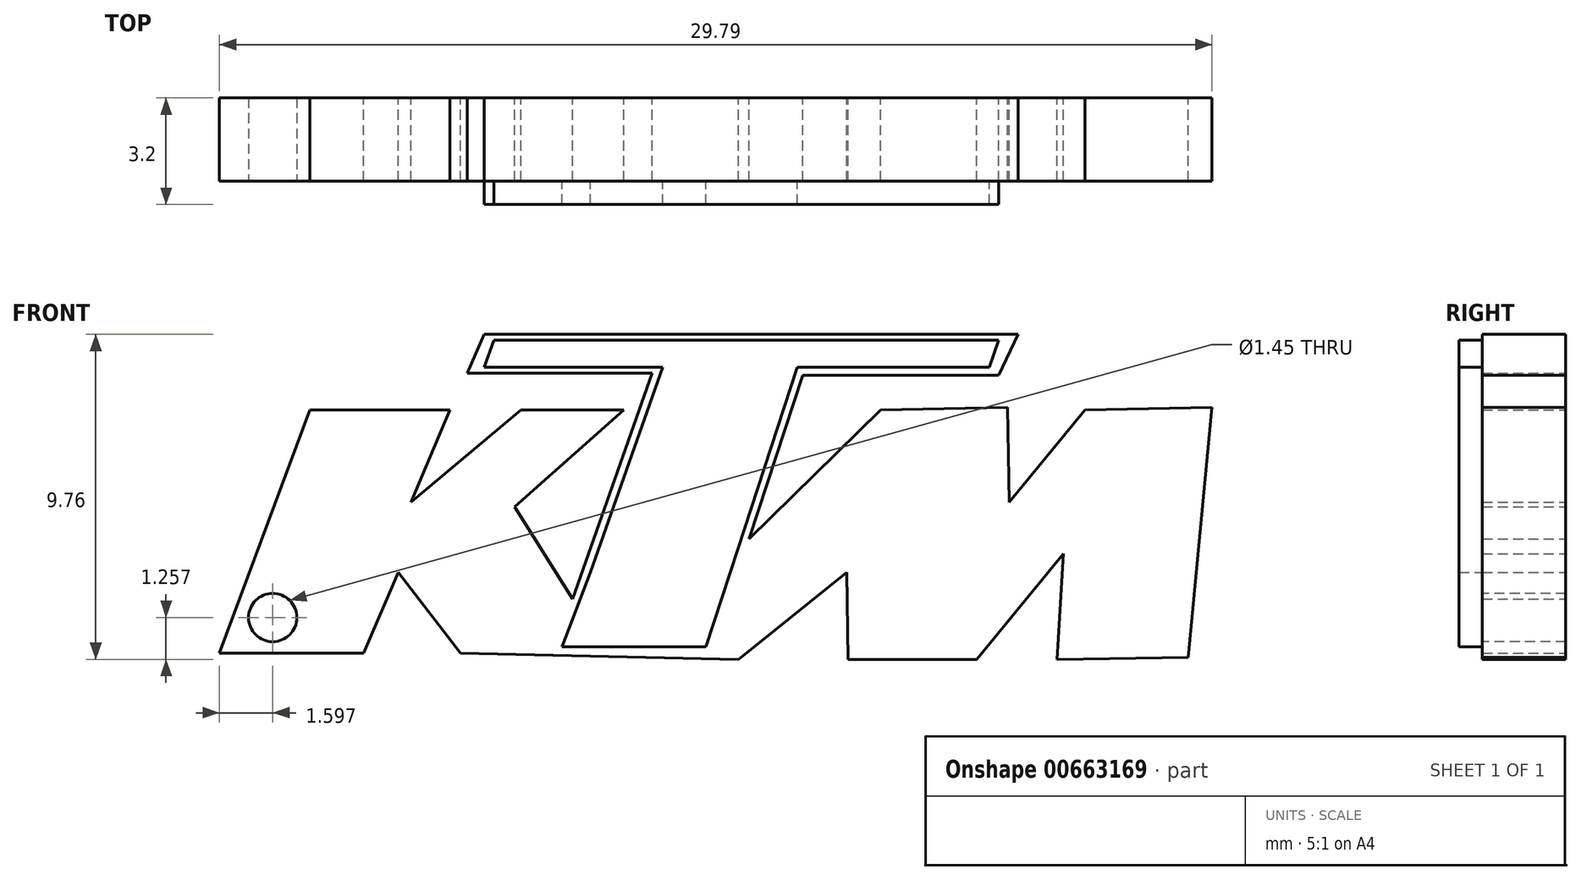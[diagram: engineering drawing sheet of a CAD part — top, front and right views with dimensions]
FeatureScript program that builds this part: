
annotation { "Feature Type Name" : "Feature", "Feature Type Description" : "" }
export const myFeature = defineFeature(function(context is Context, id is Id, definition is map)
    precondition{}
    {
        {
            var Q0;
            Q0=qCreatedBy(makeId("Front.planeOp"),FACE);
            var sketch = newSketch(context, id + "F0", { "sketchPlane" : qUnion([Q0])});
            skLineSegment(sketch, "E0", {"start": v(-12.13, -2.42) * mm, "end": v(-9.42, 4.88) * mm});
            skLineSegment(sketch, "E1", {"start": v(-9.42, 4.88) * mm, "end": v(-5.22, 4.88) * mm});
            skLineSegment(sketch, "E2", {"start": v(-5.22, 4.88) * mm, "end": v(-6.38, 2.1) * mm});
            skLineSegment(sketch, "E3", {"start": v(-6.38, 2.1) * mm, "end": v(-3.08, 4.88) * mm});
            skLineSegment(sketch, "E4", {"start": v(-3.08, 4.88) * mm, "end": v(0, 4.88) * mm});
            skLineSegment(sketch, "E5", {"start": v(0, 4.88) * mm, "end": v(-3.28, 1.98) * mm});
            skLineSegment(sketch, "E6", {"start": v(-3.28, 1.98) * mm, "end": v(-1.53, -0.8) * mm});
            skLineSegment(sketch, "E7", {"start": v(-1.53, -0.8) * mm, "end": v(0.86, 5.98) * mm});
            skLineSegment(sketch, "E8", {"start": v(0.86, 5.98) * mm, "end": v(-4.7, 5.98) * mm});
            skLineSegment(sketch, "E9", {"start": v(-4.7, 5.98) * mm, "end": v(-4.18, 7.15) * mm});
            skLineSegment(sketch, "E10", {"start": v(-4.18, 7.15) * mm, "end": v(11.84, 7.15) * mm});
            skLineSegment(sketch, "E11", {"start": v(11.84, 7.15) * mm, "end": v(11.26, 5.92) * mm});
            skLineSegment(sketch, "E12", {"start": v(11.26, 5.92) * mm, "end": v(5.38, 5.92) * mm});
            skLineSegment(sketch, "E13", {"start": v(5.38, 5.92) * mm, "end": v(3.77, 1) * mm});
            skLineSegment(sketch, "E14", {"start": v(3.77, 1) * mm, "end": v(7.7, 4.88) * mm});
            skLineSegment(sketch, "E15", {"start": v(11.52, 4.95) * mm, "end": v(7.7, 4.88) * mm});
            skLineSegment(sketch, "E16", {"start": v(11.52, 4.95) * mm, "end": v(11.57, 2.11) * mm});
            skLineSegment(sketch, "E17", {"start": v(11.57, 2.11) * mm, "end": v(13.85, 4.88) * mm});
            skLineSegment(sketch, "E18", {"start": v(13.85, 4.88) * mm, "end": v(17.66, 4.95) * mm});
            skLineSegment(sketch, "E19", {"start": v(17.66, 4.95) * mm, "end": v(16.95, -2.55) * mm});
            skLineSegment(sketch, "E20", {"start": v(16.95, -2.55) * mm, "end": v(13.01, -2.61) * mm});
            skLineSegment(sketch, "E21", {"start": v(13.2, 0.56) * mm, "end": v(13.01, -2.61) * mm});
            skLineSegment(sketch, "E22", {"start": v(13.2, 0.56) * mm, "end": v(10.6, -2.61) * mm});
            skLineSegment(sketch, "E23", {"start": v(6.74, -2.61) * mm, "end": v(10.6, -2.61) * mm});
            skLineSegment(sketch, "E24", {"start": v(6.74, -2.61) * mm, "end": v(6.7, 0) * mm});
            skLineSegment(sketch, "E25", {"start": v(6.7, 0) * mm, "end": v(3.44, -2.61) * mm});
            skLineSegment(sketch, "E26", {"start": v(-4.9, -2.42) * mm, "end": v(3.44, -2.61) * mm});
            skLineSegment(sketch, "E27", {"start": v(-6.77, 0) * mm, "end": v(-4.9, -2.42) * mm});
            skLineSegment(sketch, "E28", {"start": v(-7.8, -2.42) * mm, "end": v(-6.77, 0) * mm});
            skLineSegment(sketch, "E29", {"start": v(-12.13, -2.42) * mm, "end": v(-7.8, -2.42) * mm});
            skSolve(sketch);
        }
        {
            var Q0;
            Q0=makeQuery(id+"F0.imprint","IMPRINT",FACE,{"disambiguationData":[TD([[makeQuery(id+"F0.imprint","IMPRINT",EDGE,{"derivedFrom":sQuery(id+"F0.wireOp",EDGE,"E0")}),-1.0]])]});
            extrude(context, id + "F1", {"entities" : qUnion([Q0]), "depth" : 2.5 * mm, "offsetDistance" : 25 * mm});
        }
        {
            var Q0;
            Q0=makeQuery(id+"F1.opExtrude","CAP_FACE",FACE,{"disambiguationData":[OSD([sQuery(id+"F0.wireOp",EDGE,"E0"),sQuery(id+"F0.wireOp",EDGE,"E1"),sQuery(id+"F0.wireOp",EDGE,"E2"),sQuery(id+"F0.wireOp",EDGE,"E3"),sQuery(id+"F0.wireOp",EDGE,"E4"),sQuery(id+"F0.wireOp",EDGE,"E5"),sQuery(id+"F0.wireOp",EDGE,"E6"),sQuery(id+"F0.wireOp",EDGE,"E7"),sQuery(id+"F0.wireOp",EDGE,"E8"),sQuery(id+"F0.wireOp",EDGE,"E9"),sQuery(id+"F0.wireOp",EDGE,"E10"),sQuery(id+"F0.wireOp",EDGE,"E11"),sQuery(id+"F0.wireOp",EDGE,"E12"),sQuery(id+"F0.wireOp",EDGE,"E13"),sQuery(id+"F0.wireOp",EDGE,"E14"),sQuery(id+"F0.wireOp",EDGE,"E15"),sQuery(id+"F0.wireOp",EDGE,"E16"),sQuery(id+"F0.wireOp",EDGE,"E17"),sQuery(id+"F0.wireOp",EDGE,"E18"),sQuery(id+"F0.wireOp",EDGE,"E19"),sQuery(id+"F0.wireOp",EDGE,"E20"),sQuery(id+"F0.wireOp",EDGE,"E21"),sQuery(id+"F0.wireOp",EDGE,"E22"),sQuery(id+"F0.wireOp",EDGE,"E23"),sQuery(id+"F0.wireOp",EDGE,"E24"),sQuery(id+"F0.wireOp",EDGE,"E25"),sQuery(id+"F0.wireOp",EDGE,"E26"),sQuery(id+"F0.wireOp",EDGE,"E27"),sQuery(id+"F0.wireOp",EDGE,"E28"),sQuery(id+"F0.wireOp",EDGE,"E29")])],"isStart":false});
            var sketch = newSketch(context, id + "F2", { "sketchPlane" : qUnion([Q0])});
            skCircle(sketch, "E30", {"center": v(-10.53, -1.35) * mm, "radius": 0.72 * mm});
            skSolve(sketch);
        }
        {
            var Q0;
            Q0 = qSketchRegion(id + "F2", true);
            extrude(context, id + "F3", {"entities" : qUnion([Q0]), "operationType" : NewBodyOperationType.REMOVE, "endBound" : BoundingType.UP_TO_NEXT, "oppositeDirection" : true, "depth" : 25 * mm, "offsetDistance" : 25 * mm});
        }
        {
            var Q0;
            Q0=makeQuery(id+"F1.opExtrude","CAP_FACE",FACE,{"disambiguationData":[OSD([sQuery(id+"F0.wireOp",EDGE,"E0"),sQuery(id+"F0.wireOp",EDGE,"E1"),sQuery(id+"F0.wireOp",EDGE,"E2"),sQuery(id+"F0.wireOp",EDGE,"E3"),sQuery(id+"F0.wireOp",EDGE,"E4"),sQuery(id+"F0.wireOp",EDGE,"E5"),sQuery(id+"F0.wireOp",EDGE,"E6"),sQuery(id+"F0.wireOp",EDGE,"E7"),sQuery(id+"F0.wireOp",EDGE,"E8"),sQuery(id+"F0.wireOp",EDGE,"E9"),sQuery(id+"F0.wireOp",EDGE,"E10"),sQuery(id+"F0.wireOp",EDGE,"E11"),sQuery(id+"F0.wireOp",EDGE,"E12"),sQuery(id+"F0.wireOp",EDGE,"E13"),sQuery(id+"F0.wireOp",EDGE,"E14"),sQuery(id+"F0.wireOp",EDGE,"E15"),sQuery(id+"F0.wireOp",EDGE,"E16"),sQuery(id+"F0.wireOp",EDGE,"E17"),sQuery(id+"F0.wireOp",EDGE,"E18"),sQuery(id+"F0.wireOp",EDGE,"E19"),sQuery(id+"F0.wireOp",EDGE,"E20"),sQuery(id+"F0.wireOp",EDGE,"E21"),sQuery(id+"F0.wireOp",EDGE,"E22"),sQuery(id+"F0.wireOp",EDGE,"E23"),sQuery(id+"F0.wireOp",EDGE,"E24"),sQuery(id+"F0.wireOp",EDGE,"E25"),sQuery(id+"F0.wireOp",EDGE,"E26"),sQuery(id+"F0.wireOp",EDGE,"E27"),sQuery(id+"F0.wireOp",EDGE,"E28"),sQuery(id+"F0.wireOp",EDGE,"E29")])],"isStart":false});
            var sketch = newSketch(context, id + "F4", { "sketchPlane" : qUnion([Q0])});
            skLineSegment(sketch, "E31", {"start": v(-3.5, 6.98) * mm, "end": v(11.13, 6.98) * mm});
            skLineSegment(sketch, "E32", {"start": v(-3.5, 6.98) * mm, "end": v(-3.78, 6.98) * mm});
            skLineSegment(sketch, "E33", {"start": v(-4.06, 6.16) * mm, "end": v(-1.22, 6.16) * mm});
            skLineSegment(sketch, "E34", {"start": v(-1.22, 6.16) * mm, "end": v(1.06, 6.16) * mm});
            skLineSegment(sketch, "E35", {"start": v(11.13, 6.98) * mm, "end": v(11.26, 6.98) * mm});
            skLineSegment(sketch, "E36", {"start": v(11.26, 6.98) * mm, "end": v(10.97, 6.16) * mm});
            skLineSegment(sketch, "E37", {"start": v(10.97, 6.16) * mm, "end": v(5.46, 6.16) * mm});
            skLineSegment(sketch, "E38", {"start": v(5.46, 6.16) * mm, "end": v(5.22, 6.16) * mm});
            skLineSegment(sketch, "E39", {"start": v(-4.18, 6.16) * mm, "end": v(-4.06, 6.16) * mm});
            skLineSegment(sketch, "E40", {"start": v(-4.18, 6.16) * mm, "end": v(-3.9, 6.98) * mm});
            skLineSegment(sketch, "E41", {"start": v(-3.78, 6.98) * mm, "end": v(-3.9, 6.98) * mm});
            skLineSegment(sketch, "E42", {"start": v(5.22, 6.16) * mm, "end": v(3.44, 0.72) * mm});
            skLineSegment(sketch, "E43", {"start": v(1.06, 6.16) * mm, "end": v(1.18, 6.16) * mm});
            skLineSegment(sketch, "E44", {"start": v(1.18, 6.16) * mm, "end": v(-1, 0) * mm});
            skLineSegment(sketch, "E45", {"start": v(-1, 0) * mm, "end": v(-1.53, -1.4) * mm});
            skLineSegment(sketch, "E46", {"start": v(-1.53, -1.4) * mm, "end": v(-1.85, -2.23) * mm});
            skLineSegment(sketch, "E47", {"start": v(3.44, 0.72) * mm, "end": v(2.47, -2.23) * mm});
            skLineSegment(sketch, "E48", {"start": v(2.47, -2.23) * mm, "end": v(-1.85, -2.23) * mm});
            skSolve(sketch);
        }
        {
            var Q0;
            Q0=makeQuery(id+"F4.imprint","IMPRINT",FACE,{"disambiguationData":[TD([[makeQuery(id+"F4.imprint","IMPRINT",EDGE,{"derivedFrom":sQuery(id+"F4.wireOp",EDGE,"E31")}),-1.0]])]});
            extrude(context, id + "F5", {"entities" : qUnion([Q0]), "operationType" : NewBodyOperationType.ADD, "depth" : 0.7 * mm, "offsetDistance" : 25 * mm});
        }
    });
